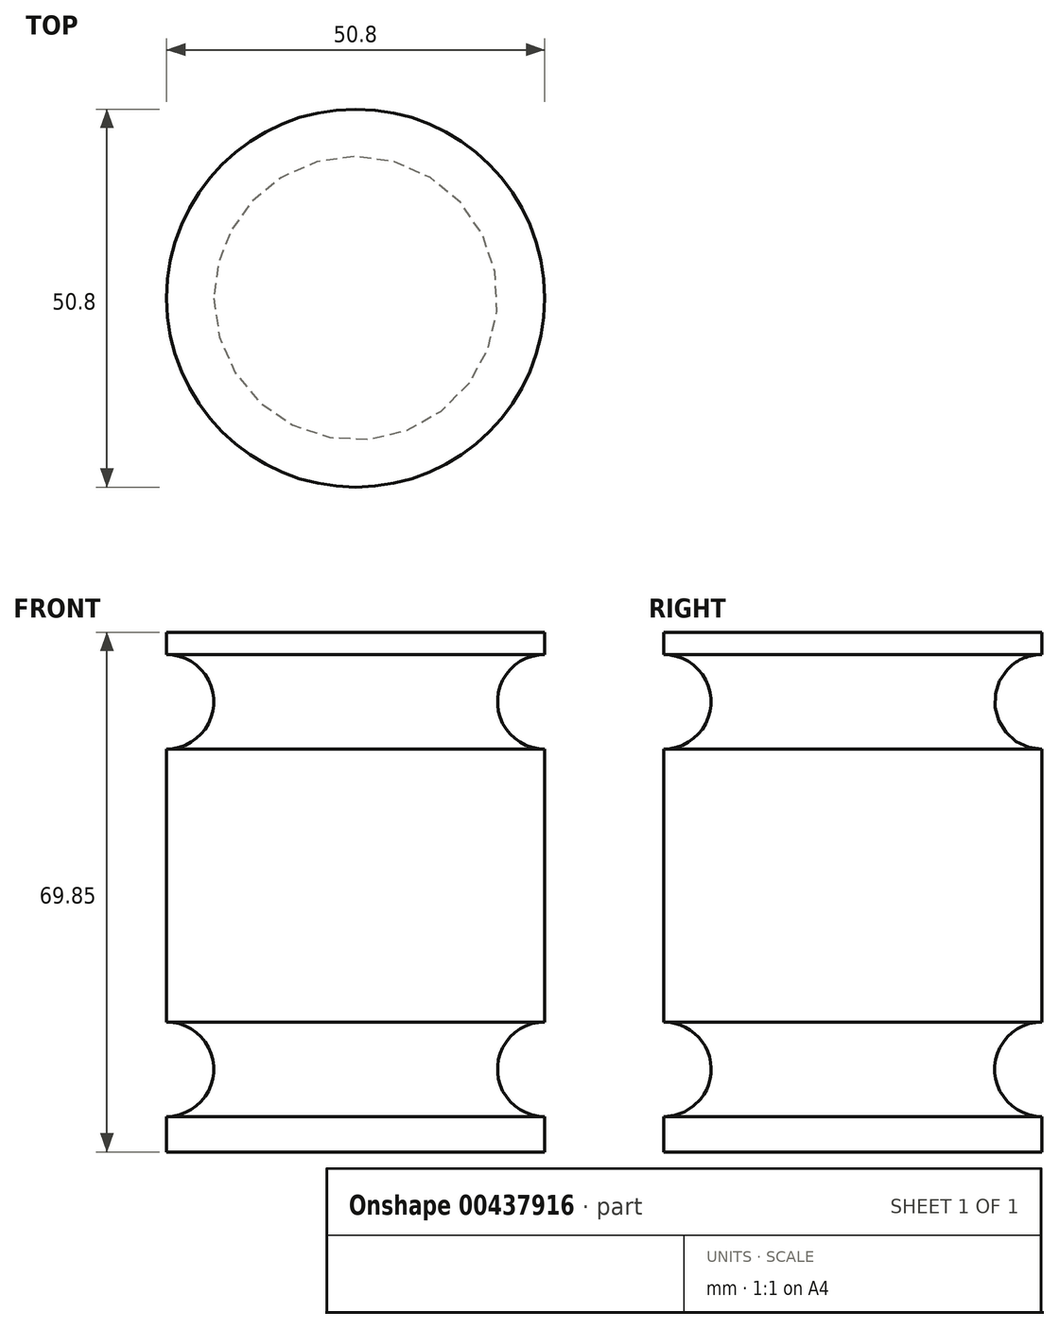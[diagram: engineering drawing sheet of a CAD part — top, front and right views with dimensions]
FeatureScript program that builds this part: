
annotation { "Feature Type Name" : "Feature", "Feature Type Description" : "" }
export const myFeature = defineFeature(function(context is Context, id is Id, definition is map)
    precondition{}
    {
        {
            var Q0;
            Q0=qCreatedBy(makeId("Front.planeOp"),FACE);
            var sketch = newSketch(context, id + "F0", { "sketchPlane" : qUnion([Q0])});
            skLineSegment(sketch, "E0.bottom", {"start": v(0, 0) * mm, "end": v(25.4, 0) * mm});
            skLineSegment(sketch, "E0.top", {"start": v(0, 69.85) * mm, "end": v(25.4, 69.85) * mm});
            skLineSegment(sketch, "E0.left", {"start": v(0, 0) * mm, "end": v(0, 69.85) * mm});
            skLineSegment(sketch, "E0.right", {"start": v(25.4, 0) * mm, "end": v(25.4, 4.75) * mm});
            skArc(sketch, "E1", {"start": v(25.4, 66.85) * mm, "mid": v(19.05, 60.5) * mm, "end": v(25.4, 54.15) * mm});
            skArc(sketch, "E2", {"start": v(25.4, 17.45) * mm, "mid": v(19.05, 11.1) * mm, "end": v(25.4, 4.75) * mm});
            skLineSegment(sketch, "E3.trimOffspring", {"start": v(25.4, 17.45) * mm, "end": v(25.4, 54.15) * mm});
            skLineSegment(sketch, "E4.trimOffspring", {"start": v(25.4, 66.85) * mm, "end": v(25.4, 69.85) * mm});
            skSolve(sketch);
        }
        {
            var Q0;
            Q0 = qSketchRegion(id + "F0", true);
            var Q1;
            Q1=sQuery(id+"F0.wireOp",EDGE,"E0.left");
            revolve(context, id + "F1", {"entities" : qUnion([Q0]), "axis" : qUnion([Q1]), "revolveType" : RevolveType.FULL});
        }
    });
